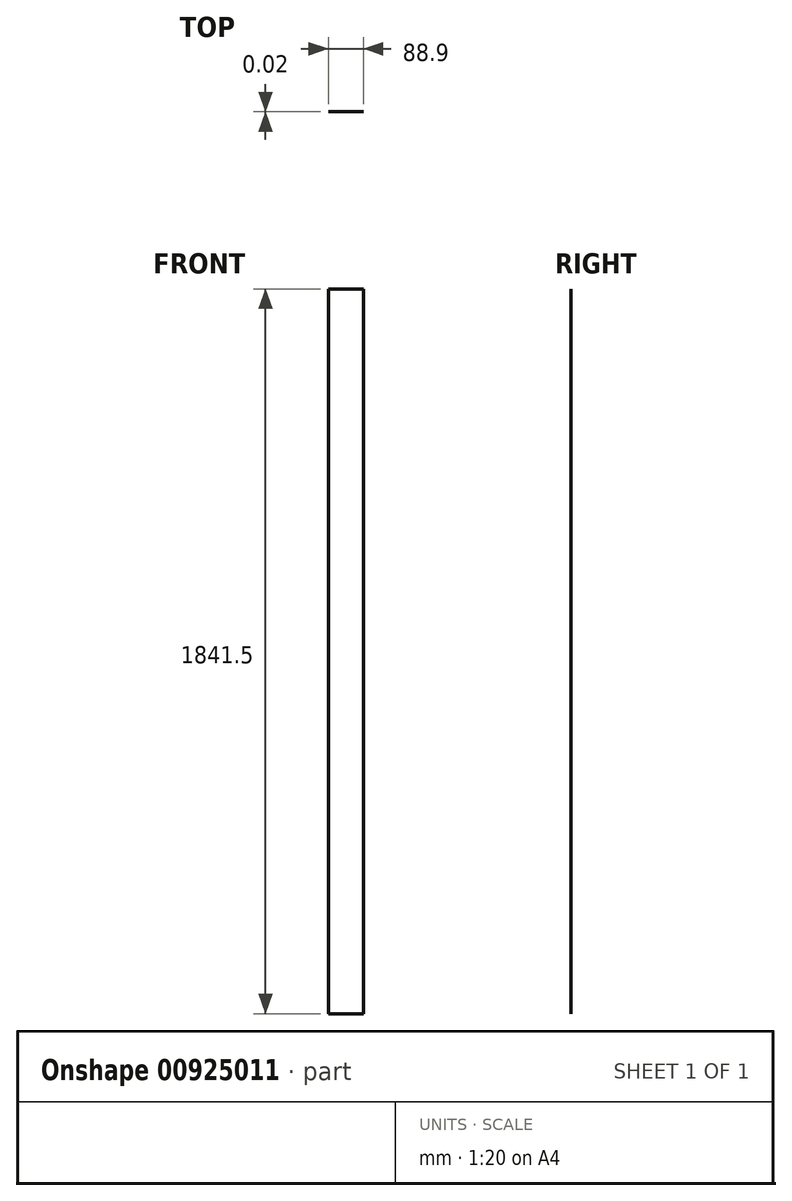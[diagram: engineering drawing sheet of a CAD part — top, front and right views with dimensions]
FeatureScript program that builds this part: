
annotation { "Feature Type Name" : "Feature", "Feature Type Description" : "" }
export const myFeature = defineFeature(function(context is Context, id is Id, definition is map)
    precondition{}
    {
        {
            var Q0;
            Q0=qCreatedBy(makeId("Front.planeOp"),FACE);
            var sketch = newSketch(context, id + "F0", { "sketchPlane" : qUnion([Q0])});
            skLineSegment(sketch, "E0.bottom", {"start": v(0, 0) * mm, "end": v(88.9, 0) * mm});
            skLineSegment(sketch, "E0.top", {"start": v(0, 1841.5) * mm, "end": v(88.9, 1841.5) * mm});
            skLineSegment(sketch, "E0.left", {"start": v(0, 0) * mm, "end": v(0, 1841.5) * mm});
            skLineSegment(sketch, "E0.right", {"start": v(88.9, 0) * mm, "end": v(88.9, 1841.5) * mm});
            skSolve(sketch);
        }
        {
            var Q0;
            Q0 = qSketchRegion(id + "F0", true);
            extrude(context, id + "F1", {"entities" : qUnion([Q0]), "depth" : 5 / 203.2 * mm, "offsetDistance" : 25.4 * mm});
        }
        {
            var Q0;
            Q0=qCreatedBy(makeId("Top.planeOp"),FACE);
            var sketch = newSketch(context, id + "F2", { "sketchPlane" : qUnion([Q0])});
            skArc(sketch, "E1", {"start": v(34.93, -15.88) * mm, "mid": v(28.58, -9.52) * mm, "end": v(22.23, -15.88) * mm});
            skArc(sketch, "E2", {"start": v(66.68, -15.88) * mm, "mid": v(60.33, -9.52) * mm, "end": v(53.98, -15.88) * mm});
            skLineSegment(sketch, "E3", {"start": v(22.23, -15.88) * mm, "end": v(34.93, -15.88) * mm});
            skLineSegment(sketch, "E4", {"start": v(53.98, -15.88) * mm, "end": v(66.68, -15.88) * mm});
            skSolve(sketch);
        }
        {
            var Q0;
            Q0=makeQuery(id+"F2.imprint","IMPRINT",FACE,{"disambiguationData":[TD([[makeQuery(id+"F2.imprint","IMPRINT",EDGE,{"derivedFrom":sQuery(id+"F2.wireOp",EDGE,"E1")}),1.0]])]});
            var Q1;
            Q1=makeQuery(id+"F2.imprint","IMPRINT",FACE,{"disambiguationData":[TD([[makeQuery(id+"F2.imprint","IMPRINT",EDGE,{"derivedFrom":sQuery(id+"F2.wireOp",EDGE,"E2")}),1.0]])]});
            extrude(context, id + "F3", {"entities" : qUnion([Q0, Q1]), "operationType" : NewBodyOperationType.REMOVE, "depth" : 1841.5 * mm, "offsetDistance" : 25.4 * mm});
        }
    });
